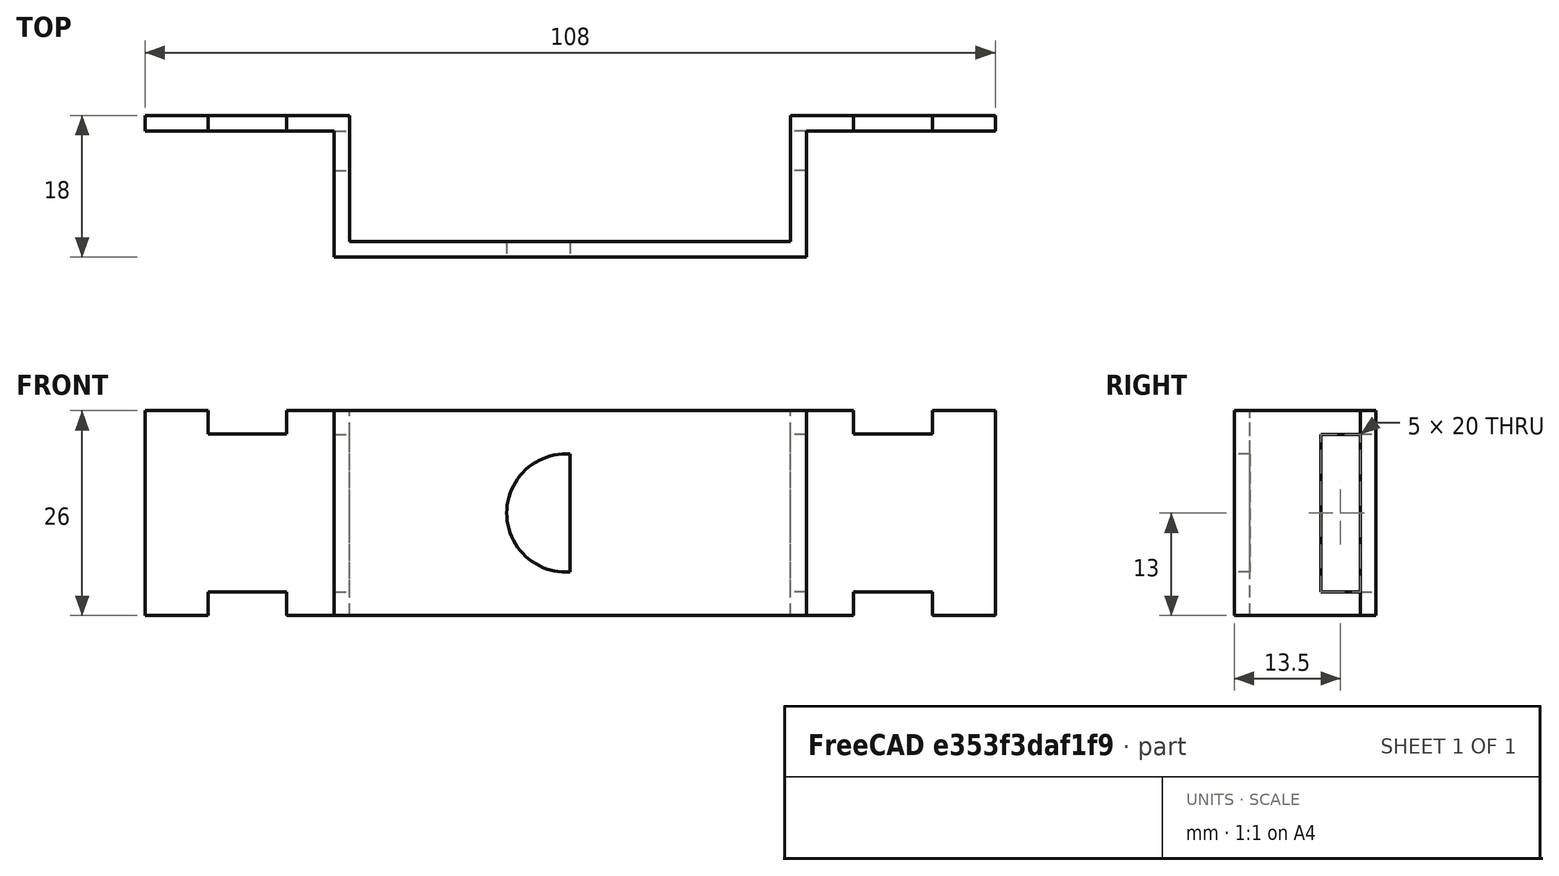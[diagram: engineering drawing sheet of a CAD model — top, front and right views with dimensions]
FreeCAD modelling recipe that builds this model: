
FCSTD DOCUMENT  (FreeCAD 0.19R17421 +113 (Git))
Label: serrure grille
License: All rights reserved
LicenseURL: http://en.wikipedia.org/wiki/All_rights_reserved
objects: TechDraw::DrawViewDimension×9, Sketcher::SketchObject×5, PartDesign::Mirrored×4, TechDraw::DrawViewPart×4, PartDesign::Plane×3, PartDesign::Pocket×3, PartDesign::Pad×1, PartDesign::Body×1, TechDraw::DrawSVGTemplate×1, TechDraw::DrawPage×1
note: 21 computed .brp shape members not serialized (recipe doc carries the construction recipe); baked Part::Feature solids carry a one-line shape summary decoded from their .brp

FEATURE [Sketcher::SketchObject] Sketch
  MapMode = 5
  Support = -> [XY_Plane]
  sketch-geometry (8):
    g0: LineSegment StartX=-54 StartY=0 StartZ=0 EndX=-28 EndY=0 EndZ=0
    g1: LineSegment StartX=-28 StartY=0 StartZ=0 EndX=-28 EndY=-16 EndZ=0
    g2: LineSegment StartX=-28 StartY=-16 StartZ=0 EndX=0 EndY=-16 EndZ=0
    g3: LineSegment StartX=-54 StartY=0 StartZ=0 EndX=-54 EndY=-2 EndZ=0
    g4: LineSegment StartX=-54 StartY=-2 StartZ=0 EndX=-30 EndY=-2 EndZ=0
    g5: LineSegment StartX=-30 StartY=-2 StartZ=0 EndX=-30 EndY=-18 EndZ=0
    g6: LineSegment StartX=-30 StartY=-18 StartZ=0 EndX=0 EndY=-18 EndZ=0
    g7: LineSegment StartX=0 StartY=-18 StartZ=0 EndX=0 EndY=-16 EndZ=0
  constraints (24):
    c: Horizontal(g0)
    c: Coincident(g1,g0)
    c: Vertical(g1)
    c: Coincident(g2,g1)
    c: Horizontal(g2)
    c: DistanceX(g0,g0) = 26
    c: Coincident(g3,g4)
    c: Horizontal(g4)
    c: Coincident(g4,g5)
    c: Vertical(g5)
    c: Coincident(g5,g6)
    c: Horizontal(g6)
    c: Coincident(g6,g7)
    c: Coincident(g7,g2)
    c: DistanceY(g3,g3) = 2
    c: DistanceY(g5,g1) = 2
    c: DistanceX(g4,g0) = 2
    c: DistanceY(g6,g0) = 18
    c: DistanceX(g6,g6) = 30
    c: Vertical(g7)
    c: Coincident(g0,g3)
    c: Vertical(g3)
    c: PointOnObject(g0,g-1)
    c: PointOnObject(g2,g-2)
FEATURE [PartDesign::Pad] Pad
  Length = 26
  Length2 = 100
  Profile = -> Sketch
  Type = 0
FEATURE [PartDesign::Plane] DatumPlane
  Length = 34.3498
  MapMode = 5
  Placement = pos=(-30,0,0) rot=(0.57735,-0.57735,-0.57735;2.0944rad)
  ResizeMode = 0
  Support = -> [Pad]
  Width = 42.3498
FEATURE [Sketcher::SketchObject] Sketch001
  MapMode = 5
  Support = -> [XY_Plane]
FEATURE [Sketcher::SketchObject] Sketch002
  MapMode = 5
  Placement = pos=(-30,0,0) rot=(0.57735,-0.57735,-0.57735;2.0944rad)
  Support = -> [DatumPlane]
  sketch-geometry (4):
    g0: LineSegment StartX=7 StartY=23 StartZ=0 EndX=2 EndY=23 EndZ=0
    g1: LineSegment StartX=2 StartY=23 StartZ=0 EndX=2 EndY=3 EndZ=0
    g2: LineSegment StartX=2 StartY=3 StartZ=0 EndX=7 EndY=3 EndZ=0
    g3: LineSegment StartX=7 StartY=3 StartZ=0 EndX=7 EndY=23 EndZ=0
  constraints (12):
    c: Coincident(g0,g1)
    c: Coincident(g1,g2)
    c: Coincident(g2,g3)
    c: Coincident(g3,g0)
    c: Horizontal(g0)
    c: Horizontal(g2)
    c: Vertical(g1)
    c: Vertical(g3)
    c: DistanceX(g-1,g1) = 2
    c: DistanceY(g-1,g2) = 3
    c: DistanceX(g0,g0) = 5
    c: DistanceY(g3,g3) = 20
FEATURE [PartDesign::Pocket] Pocket
  BaseFeature = -> Pad
  Length = 5
  Length2 = 100
  Profile = -> Sketch002
  Type = 1
FEATURE [PartDesign::Plane] DatumPlane001
  Length = 120.471
  MapMode = 5
  Placement = pos=(0,-2,0) rot=(1,0,0;1.5708rad)
  ResizeMode = 0
  Support = -> [Pocket]
  Width = 48.4708
FEATURE [Sketcher::SketchObject] Sketch004
  MapMode = 5
  Placement = pos=(0,-2,0) rot=(1,0,0;1.5708rad)
  Support = -> [DatumPlane001]
  sketch-geometry (9):
    g0: LineSegment StartX=-46 StartY=26.0395 StartZ=0 EndX=-36 EndY=26.0395 EndZ=0
    g1: LineSegment StartX=-36 StartY=26.0395 StartZ=0 EndX=-36 EndY=23.0395 EndZ=0
    g2: LineSegment StartX=-36 StartY=23.0395 StartZ=0 EndX=-46 EndY=23.0395 EndZ=0
    g3: LineSegment StartX=-46 StartY=23.0395 StartZ=0 EndX=-46 EndY=26.0395 EndZ=0
    g4: LineSegment StartX=-46 StartY=3 StartZ=0 EndX=-36 EndY=3 EndZ=0
    g5: LineSegment StartX=-36 StartY=3 StartZ=0 EndX=-36 EndY=0 EndZ=0
    g6: LineSegment StartX=-36 StartY=0 StartZ=0 EndX=-46 EndY=0 EndZ=0
    g7: LineSegment StartX=-46 StartY=0 StartZ=0 EndX=-46 EndY=3 EndZ=0
    g8: LineSegment [constr] StartX=-46 StartY=45.6632 StartZ=0 EndX=-46 EndY=-30.8295 EndZ=0
  constraints (25):
    c: Coincident(g0,g1)
    c: Coincident(g1,g2)
    c: Coincident(g2,g3)
    c: Coincident(g3,g0)
    c: Horizontal(g0)
    c: Horizontal(g2)
    c: Vertical(g1)
    c: Vertical(g3)
    c: Coincident(g4,g5)
    c: Coincident(g5,g6)
    c: Coincident(g6,g7)
    c: Coincident(g7,g4)
    c: Horizontal(g4)
    c: Horizontal(g6)
    c: Vertical(g5)
    c: Vertical(g7)
    c: DistanceX(g0,g0) = 10
    c: DistanceX(g4,g4) = 10
    c: DistanceY(g1,g1) = 3
    c: DistanceY(g5,g5) = 3
    c: PointOnObject(g5,g-1)
    c: DistanceX(g5,g-1) = 36
    c: Vertical(g8)
    c: PointOnObject(g4,g8)
    c: PointOnObject(g0,g8)
FEATURE [PartDesign::Pocket] Pocket001
  BaseFeature = -> Pocket
  Length = 5
  Length2 = 100
  Profile = -> Sketch004
  Type = 0
FEATURE [PartDesign::Plane] DatumPlane002
  Length = 120.471
  MapMode = 5
  Placement = pos=(0,-18,0) rot=(1,0,0;1.5708rad)
  ResizeMode = 0
  Support = -> [Pocket001]
  Width = 48.4708
FEATURE [Sketcher::SketchObject] Sketch005
  MapMode = 5
  Placement = pos=(0,-18,0) rot=(1,0,0;1.5708rad)
  Support = -> [DatumPlane002]
  sketch-geometry (1):
    g0: Circle CenterX=-0.570245 CenterY=13 CenterZ=0 NormalX=0 NormalY=0 NormalZ=1 AngleXU=0 Radius=7.5
  constraints (2):
    c: Diameter(g0) = 15
    c: DistanceY(g-1,g0) = 13
FEATURE [PartDesign::Pocket] Pocket002
  BaseFeature = -> Pocket001
  Length = 5
  Length2 = 100
  Profile = -> Sketch005
  Type = 0
FEATURE [PartDesign::Mirrored] Mirrored
  BaseFeature = -> Pocket002
  MirrorPlane = -> Sketch [V_Axis]
  Originals = -> [Pad]
FEATURE [PartDesign::Mirrored] Mirrored001
  BaseFeature = -> Mirrored
  MirrorPlane = -> YZ_Plane
  Originals = -> [Pocket]
FEATURE [PartDesign::Mirrored] Mirrored002
  BaseFeature = -> Mirrored001
  MirrorPlane = -> Sketch004 [V_Axis]
  Originals = -> [Pocket001]
FEATURE [PartDesign::Mirrored] Mirrored003
  BaseFeature = -> Mirrored002
  MirrorPlane = -> Sketch005 [V_Axis]
  Originals = -> [Pocket002]
FEATURE [PartDesign::Body] Body
  Group = -> [Sketch,Pad,DatumPlane,Sketch001,Sketch002,Pocket,DatumPlane001,Sketch004,Pocket001,DatumPlane002,Sketch005,Pocket002,Mirrored,Mirrored001,Mirrored002,Mirrored003]
  Origin = -> Origin
  Tip = -> Mirrored002
FEATURE [TechDraw::DrawSVGTemplate] Template
  EditableTexts = Designed_by_Name=Designed by Name; Drawing_number=Drawing number; FC-Date=Date; FC-SC=Scale; FC-SH=Sheet; FC-Title=Title; Subtitle=Subtitle; Weight=Weight
  Height = 210
  Orientation = 1
  Width = 297
FEATURE [TechDraw::DrawViewPart] View
  CoarseView = false
  Direction = (-0.139,-0.448,0.883)
  Focus = 100
  HardHidden = false
  IsoCount = 0
  IsoHidden = false
  IsoVisible = false
  LockPosition = false
  Perspective = false
  Rotation = 180
  ScaleType = 0
  SeamHidden = false
  SeamVisible = false
  SmoothHidden = false
  SmoothVisible = false
  Source = -> [Body]
  X = 222.633
  Y = 161.568
FEATURE [TechDraw::DrawViewPart] View001
  CoarseView = false
  Direction = (0,0,-1)
  Focus = 100
  HardHidden = false
  IsoCount = 0
  IsoHidden = false
  IsoVisible = false
  LockPosition = false
  Perspective = false
  Rotation = 0
  ScaleType = 0
  SeamHidden = false
  SeamVisible = false
  SmoothHidden = false
  SmoothVisible = false
  Source = -> [Body]
  X = 71.2675
  Y = 162.343
FEATURE [TechDraw::DrawViewPart] View002
  CoarseView = false
  Direction = (0,-1,0)
  Focus = 100
  HardHidden = false
  IsoCount = 0
  IsoHidden = false
  IsoVisible = false
  LockPosition = false
  Perspective = false
  Rotation = 0
  ScaleType = 0
  SeamHidden = false
  SeamVisible = false
  SmoothHidden = false
  SmoothVisible = false
  Source = -> [Body]
  X = 73.5923
  Y = 100.351
FEATURE [TechDraw::DrawViewPart] View003
  CoarseView = false
  Direction = (-1,0,0)
  Focus = 100
  HardHidden = false
  IsoCount = 0
  IsoHidden = false
  IsoVisible = false
  LockPosition = false
  Perspective = false
  Rotation = 0
  ScaleType = 0
  SeamHidden = false
  SeamVisible = false
  SmoothHidden = false
  SmoothVisible = false
  Source = -> [Body]
  X = 150.825
  Y = 100.867
FEATURE [TechDraw::DrawViewDimension] Dimension
  Arbitrary = false
  FormatSpec = %.2f
  LockPosition = false
  MeasureType = 1
  OverTolerance = 0
  References2D = -> [View001]
  Rotation = 0
  ScaleType = 0
  Type = 1
  UnderTolerance = 0
  X = -40.7417
  Y = -22.1734
FEATURE [TechDraw::DrawViewDimension] Dimension001
  Arbitrary = false
  FormatSpec = %.2f
  LockPosition = false
  MeasureType = 1
  OverTolerance = 0
  References2D = -> [View001]
  Rotation = 0
  ScaleType = 0
  Type = 2
  UnderTolerance = 0
  X = -43.9513
  Y = 22.6147
FEATURE [TechDraw::DrawViewDimension] Dimension002
  Arbitrary = false
  FormatSpec = %.2f
  LockPosition = false
  MeasureType = 1
  OverTolerance = 0
  References2D = -> [View001]
  Rotation = 0
  ScaleType = 0
  Type = 1
  UnderTolerance = 0
  X = -0.196497
  Y = 20.2004
FEATURE [TechDraw::DrawViewDimension] Dimension003
  Arbitrary = false
  FormatSpec = ⌀%.2f
  LockPosition = false
  MeasureType = 1
  OverTolerance = 0
  References2D = -> [View002]
  Rotation = 0
  ScaleType = 0
  Type = 5
  UnderTolerance = 0
  X = -29.4746
  Y = -27.5096
FEATURE [TechDraw::DrawViewDimension] Dimension004
  Arbitrary = false
  FormatSpec = %.2f
  LockPosition = false
  MeasureType = 1
  OverTolerance = 0
  References2D = -> [View002]
  Rotation = 0
  ScaleType = 0
  Type = 2
  UnderTolerance = 0
  X = 58.1264
  Y = 0
FEATURE [TechDraw::DrawViewDimension] Dimension005
  Arbitrary = false
  FormatSpec = %.2f
  LockPosition = false
  MeasureType = 1
  OverTolerance = 0
  References2D = -> [View003]
  Rotation = 0
  ScaleType = 0
  Type = 2
  UnderTolerance = 0
  X = 24.7237
  Y = 0
FEATURE [TechDraw::DrawViewDimension] Dimension006
  Arbitrary = false
  FormatSpec = %.2f
  LockPosition = false
  MeasureType = 1
  OverTolerance = 0
  References2D = -> [View003]
  Rotation = 0
  ScaleType = 0
  Type = 1
  UnderTolerance = 0
  X = 9.45132
  Y = -27.6848
FEATURE [TechDraw::DrawViewDimension] Dimension007
  Arbitrary = false
  FormatSpec = %.2f
  LockPosition = false
  MeasureType = 1
  OverTolerance = 0
  References2D = -> [View001]
  Rotation = 0
  ScaleType = 0
  Type = 2
  UnderTolerance = 0
  X = 63.8249
  Y = 10.6673
FEATURE [TechDraw::DrawViewDimension] Dimension008
  Arbitrary = false
  FormatSpec = %.2f
  LockPosition = false
  MeasureType = 1
  OverTolerance = 0
  References2D = -> [View002]
  Rotation = 0
  ScaleType = 0
  Type = 1
  UnderTolerance = 0
  X = -36.0487
  Y = 22.6284
FEATURE [TechDraw::DrawPage] Page
  KeepUpdated = true
  NextBalloonIndex = 1
  ProjectionType = 0
  Template = -> Template
  Views = -> [View,View001,View002,View003,Dimension,Dimension001,Dimension002,Dimension003,Dimension004,Dimension005,Dimension006,Dimension007,Dimension008]
